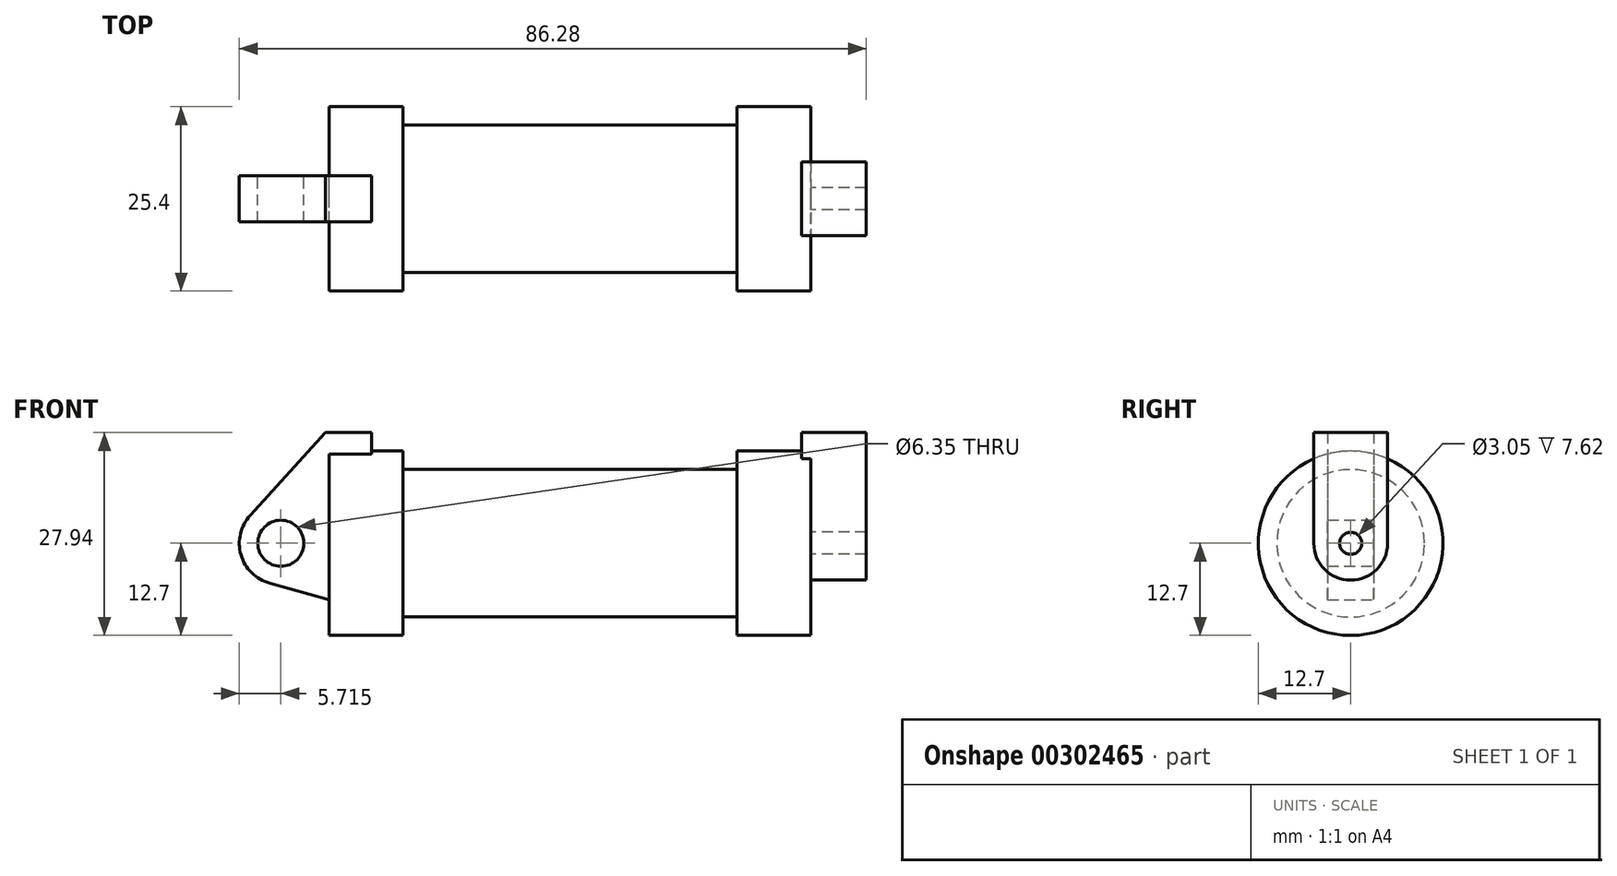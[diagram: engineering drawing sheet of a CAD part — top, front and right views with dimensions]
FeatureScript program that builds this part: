
annotation { "Feature Type Name" : "Feature", "Feature Type Description" : "" }
export const myFeature = defineFeature(function(context is Context, id is Id, definition is map)
    precondition{}
    {
        {
            var Q0;
            Q0=qCreatedBy(makeId("Front.planeOp"),FACE);
            var sketch = newSketch(context, id + "F0", { "sketchPlane" : qUnion([Q0])});
            skLineSegment(sketch, "E0", {"start": v(0, 0) * mm, "end": v(0, 12.7) * mm});
            skLineSegment(sketch, "E1", {"start": v(0, 12.7) * mm, "end": v(10.16, 12.7) * mm});
            skLineSegment(sketch, "E2", {"start": v(10.16, 12.7) * mm, "end": v(10.16, 10.16) * mm});
            skLineSegment(sketch, "E3", {"start": v(10.16, 10.16) * mm, "end": v(56.13, 10.16) * mm});
            skLineSegment(sketch, "E4", {"start": v(56.13, 10.16) * mm, "end": v(56.13, 12.7) * mm});
            skLineSegment(sketch, "E5", {"start": v(56.13, 12.7) * mm, "end": v(66.3, 12.7) * mm});
            skLineSegment(sketch, "E6", {"start": v(66.3, 12.7) * mm, "end": v(66.3, 0) * mm});
            skLineSegment(sketch, "E7", {"start": v(66.3, 0) * mm, "end": v(0, 0) * mm});
            skLineSegment(sketch, "E8", {"start": v(5.84, 15.24) * mm, "end": v(-0.5, 15.24) * mm});
            skLineSegment(sketch, "E9", {"start": v(-0.5, 15.24) * mm, "end": v(-10.88, 3.85) * mm});
            skLineSegment(sketch, "E10", {"start": v(0, 0) * mm, "end": v(-6.65, 0) * mm});
            skCircle(sketch, "E11", {"center": v(-6.65, 0) * mm, "radius": 5.72 * mm});
            skCircle(sketch, "E12", {"center": v(-6.65, 0) * mm, "radius": 3.18 * mm});
            skLineSegment(sketch, "E13", {"start": v(5.84, 15.24) * mm, "end": v(5.84, -9.4) * mm});
            skLineSegment(sketch, "E14", {"start": v(5.84, -9.4) * mm, "end": v(-8.18, -5.5) * mm});
            skSolve(sketch);
        }
        {
            var Q0;
            {var subQ0=sQuery(id+"F0.wireOp",EDGE,"E2");Q0=makeQuery(id+"F0.imprint","IMPRINT",FACE,{"disambiguationData":[TD([[makeQuery(id+"F0.imprint","IMPRINT",EDGE,{"derivedFrom":subQ0}),-1.0]])]});}
            var Q1;
            {var subQ0=sQuery(id+"F0.wireOp",EDGE,"E0");Q1=makeQuery(id+"F0.imprint","IMPRINT",FACE,{"disambiguationData":[TD([[makeQuery(id+"F0.imprint","IMPRINT",EDGE,{"derivedFrom":subQ0}),-1.0]])]});}
            var Q2;
            Q2=sQuery(id+"F0.wireOp",EDGE,"E7");
            revolve(context, id + "F1", {"entities" : qUnion([Q0, Q1]), "axis" : qUnion([Q2]), "revolveType" : RevolveType.FULL});
        }
        {
            var Q0;
            {var subQ0=sQuery(id+"F0.wireOp",EDGE,"E0");Q0=makeQuery(id+"F0.imprint","IMPRINT",FACE,{"disambiguationData":[TD([[makeQuery(id+"F0.imprint","IMPRINT",EDGE,{"derivedFrom":subQ0}),-1.0]])]});}
            var Q1;
            {var subQ1=sQuery(id+"F0.wireOp",EDGE,"E0");Q1=makeQuery(id+"F0.imprint","IMPRINT",FACE,{"disambiguationData":[TD([[makeQuery(id+"F0.imprint","IMPRINT",EDGE,{"derivedFrom":subQ1}),1.0]])]});}
            var Q2;
            {var subQ0=sQuery(id+"F0.wireOp",EDGE,"E14");Q2=makeQuery(id+"F0.imprint","IMPRINT",FACE,{"disambiguationData":[TD([[makeQuery(id+"F0.imprint","IMPRINT",EDGE,{"derivedFrom":subQ0}),-1.0]])]});}
            var Q3;
            Q3=makeQuery(id+"F0.imprint","IMPRINT",FACE,{"disambiguationData":[TD([[makeQuery(id+"F0.imprint","IMPRINT",EDGE,{"derivedFrom":sQuery(id+"F0.wireOp",EDGE,"E12")}),-1.0]])]});
            extrude(context, id + "F2", {"entities" : qUnion([Q0, Q1, Q2, Q3]), "operationType" : NewBodyOperationType.ADD, "endBound" : BoundingType.SYMMETRIC, "depth" : 6.35 * mm});
        }
        {
            var Q0;
            Q0=makeQuery(id+"F1.opRevolve","SWEPT_FACE",FACE,{"disambiguationData":[OSD([sQuery(id+"F0.wireOp",EDGE,"E6")])]});
            var sketch = newSketch(context, id + "F3", { "sketchPlane" : qUnion([Q0])});
            skCircle(sketch, "E15", {"center": v(0, 0) * mm, "radius": 1.52 * mm});
            skCircle(sketch, "E16", {"center": v(0, 0) * mm, "radius": 5.08 * mm});
            skLineSegment(sketch, "E17", {"start": v(5.08, 0) * mm, "end": v(5.08, 15.24) * mm});
            skLineSegment(sketch, "E18", {"start": v(5.08, 15.24) * mm, "end": v(-5.08, 15.24) * mm});
            skLineSegment(sketch, "E19", {"start": v(-5.08, 15.24) * mm, "end": v(-5.08, 0) * mm});
            skSolve(sketch);
        }
        {
            var Q0;
            Q0 = qSketchRegion(id + "F3", true);
            extrude(context, id + "F4", {"entities" : qUnion([Q0]), "operationType" : NewBodyOperationType.ADD, "depth" : 7.62 * mm, "hasSecondDirection" : true, "secondDirectionOppositeDirection" : true, "secondDirectionDepth" : 1.27 * mm});
        }
        {
            var Q0;
            Q0=makeQuery(id+"F4.boolean.opBoolean","SPLIT",FACE,{"disambiguationData":[TD([makeQuery(id+"F4.opExtrude","SWEPT_FACE",FACE,{"disambiguationData":[OSD([sQuery(id+"F3.wireOp",EDGE,"E15")])]})])],"derivedFrom":makeQuery(id+"F1.opRevolve","SWEPT_FACE",FACE,{"disambiguationData":[OSD([sQuery(id+"F0.wireOp",EDGE,"E6")])]})});
            var Q1;
            Q1=makeQuery(id+"F1.opRevolve","SWEPT_FACE",FACE,{"disambiguationData":[OSD([sQuery(id+"F0.wireOp",EDGE,"E2")])]});
            extrude(context, id + "F5", {"entities" : qUnion([Q0]), "operationType" : NewBodyOperationType.ADD, "endBound" : BoundingType.UP_TO_SURFACE, "oppositeDirection" : true, "endBoundEntityFace" : qUnion([Q1]), "depth" : 25.4 * mm});
        }
    });
